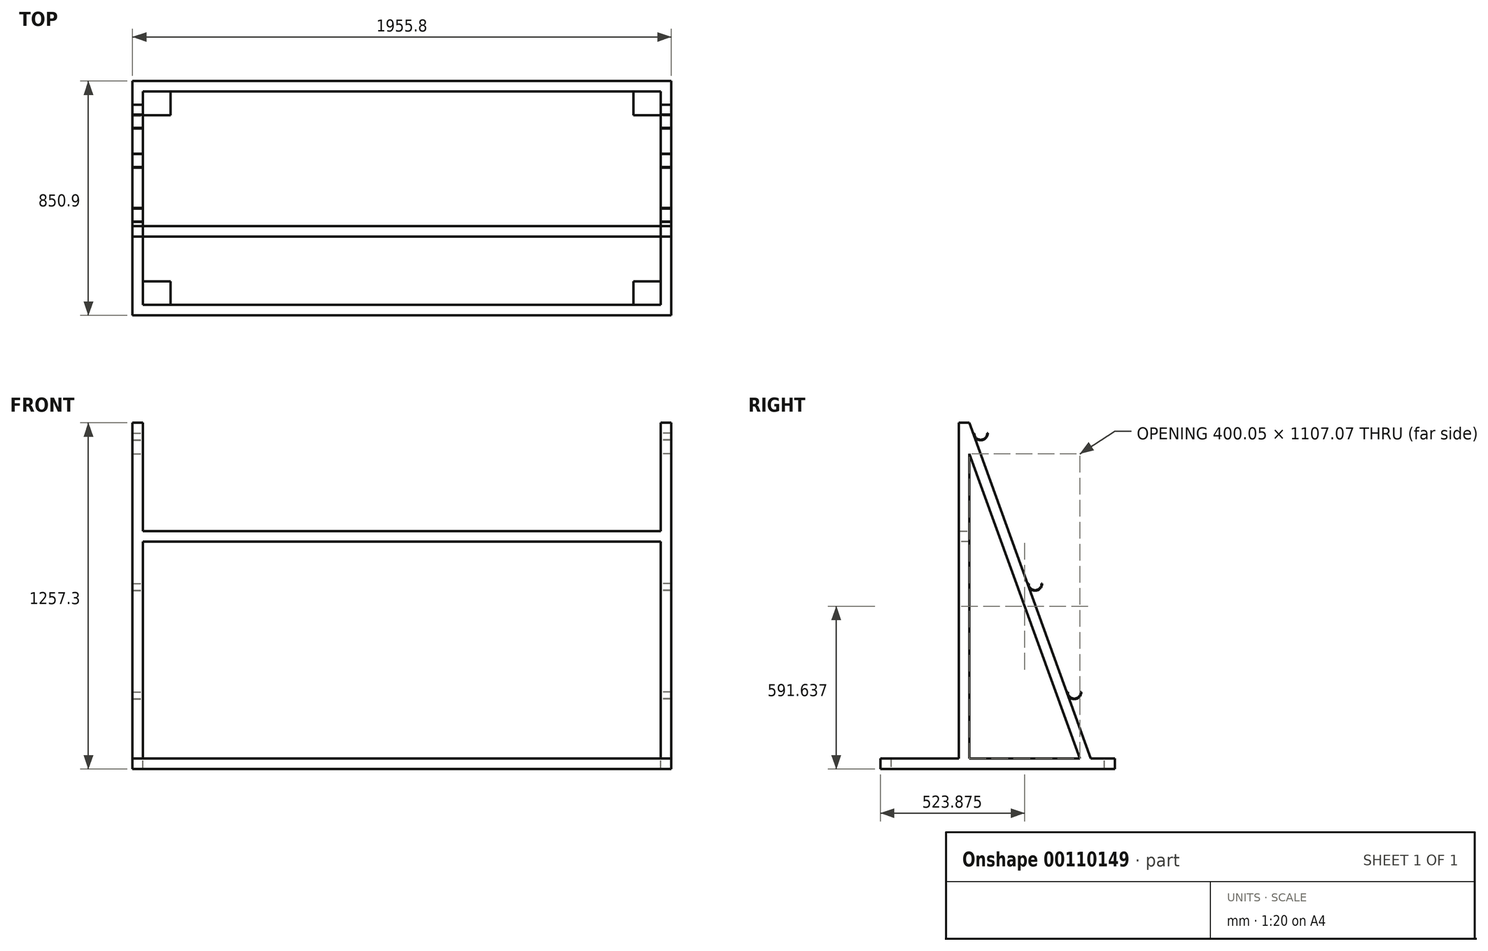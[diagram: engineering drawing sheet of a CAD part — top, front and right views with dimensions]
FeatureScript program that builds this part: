
annotation { "Feature Type Name" : "Feature", "Feature Type Description" : "" }
export const myFeature = defineFeature(function(context is Context, id is Id, definition is map)
    precondition{}
    {
        {
            var Q0;
            Q0=qCreatedBy(makeId("Right.planeOp"),FACE);
            var sketch = newSketch(context, id + "F0", { "sketchPlane" : qUnion([Q0])});
            skLineSegment(sketch, "E0", {"start": v(0, 38.1) * mm, "end": v(0, 1145.17) * mm});
            skCircle(sketch, "E1", {"center": v(40.77, 1219.2) * mm, "radius": 228.6 * mm, "construction": true});
            skLineSegment(sketch, "E2", {"start": v(-323.85, 0) * mm, "end": v(527.05, 0) * mm});
            skCircle(sketch, "E3", {"center": v(238.1, 673.1) * mm, "radius": 168.28 * mm, "construction": true});
            skCircle(sketch, "E4", {"center": v(380.37, 279.4) * mm, "radius": 168.28 * mm, "construction": true});
            skLineSegment(sketch, "E5.0", {"start": v(-38.1, 38.1) * mm, "end": v(-38.1, 1257.3) * mm});
            skLineSegment(sketch, "E6.0", {"start": v(-323.85, 38.1) * mm, "end": v(-38.1, 38.1) * mm});
            skPoint(sketch, "E7.orphan", {"position": v(0, 0) * mm});
            skLineSegment(sketch, "E8.0", {"start": v(527.05, 38.1) * mm, "end": v(527.05, 0) * mm});
            skLineSegment(sketch, "E9", {"start": v(-323.85, 38.1) * mm, "end": v(-323.85, 0) * mm});
            skLineSegment(sketch, "E10.trimOffspring", {"start": v(0, 38.1) * mm, "end": v(400.05, 38.1) * mm});
            skLineSegment(sketch, "E11.trimOffspring", {"start": v(440.56, 38.1) * mm, "end": v(527.05, 38.1) * mm});
            skLineSegment(sketch, "E12.0", {"start": v(-38.1, 1257.3) * mm, "end": v(0, 1257.3) * mm});
            skLineSegment(sketch, "E13", {"start": v(0, 1257.3) * mm, "end": v(440.56, 38.1) * mm});
            skLineSegment(sketch, "E14.0", {"start": v(0, 1145.17) * mm, "end": v(400.05, 38.1) * mm});
            skLineSegment(sketch, "E15.0", {"start": v(23.88, 1265.93) * mm, "end": v(464.45, 46.73) * mm, "construction": true});
            skLineSegment(sketch, "E16", {"start": v(40.77, 1219.2) * mm, "end": v(40.77, 1219.2) * mm});
            skLineSegment(sketch, "E17", {"start": v(238.1, 673.1) * mm, "end": v(238.1, 673.1) * mm});
            skLineSegment(sketch, "E18", {"start": v(380.37, 279.4) * mm, "end": v(380.37, 279.4) * mm});
            skSolve(sketch);
        }
        {
            var Q0;
            Q0 = qSketchRegion(id + "F0", true);
            extrude(context, id + "F1", {"entities" : qUnion([Q0]), "depth" : 38.1 * mm});
        }
        {
            var Q0;
            Q0=qCreatedBy(makeId("Right.planeOp"),FACE);
            cPlane(context, id + "F2", {"entities" : qUnion([Q0]), "cplaneType" : CPlaneType.OFFSET, "offset" : 939.8 * mm, "oppositeDirection" : true, "width" : 152.4 * mm, "height" : 152.4 * mm});
        }
        {
            var Q0;
            Q0=makeQuery(id+"F1.opExtrude","SWEPT_BODY",BODY,{"disambiguationData":[OSD([sQuery(id+"F0.wireOp",EDGE,"E0"),sQuery(id+"F0.wireOp",EDGE,"E2"),sQuery(id+"F0.wireOp",EDGE,"E5.0"),sQuery(id+"F0.wireOp",EDGE,"E6.0"),sQuery(id+"F0.wireOp",EDGE,"f51a7655-22c9-473e-9285-b1b97efc2238.0"),sQuery(id+"F0.wireOp",EDGE,"ead02582-4cc7-4f6f-915c-1df2db1e80be.0"),sQuery(id+"F0.wireOp",EDGE,"3IrbcwRK-jniz-JPX0-W7fm-mpI4lOduA6qP"),sQuery(id+"F0.wireOp",EDGE,"E8.0"),sQuery(id+"F0.wireOp",EDGE,"E9"),sQuery(id+"F0.wireOp",EDGE,"E10.trimOffspring"),sQuery(id+"F0.wireOp",EDGE,"E11.trimOffspring")])]});
            var Q1;
            Q1=qCreatedBy(id+"F2.planeOp",FACE);
            mirror(context, id + "F3", {"entities" : qUnion([Q0]), "mirrorPlane" : qUnion([Q1])});
        }
        {
            var Q0;
            Q0=qCreatedBy(makeId("Right.planeOp"),FACE);
            var sketch = newSketch(context, id + "F4", { "sketchPlane" : qUnion([Q0])});
            skLineSegment(sketch, "E19.0", {"start": v(-323.85, 38.1) * mm, "end": v(-323.85, 0) * mm});
            skLineSegment(sketch, "E20", {"start": v(-323.85, 38.1) * mm, "end": v(-285.75, 38.1) * mm});
            skLineSegment(sketch, "E21", {"start": v(-285.75, 38.1) * mm, "end": v(-285.75, 0) * mm});
            skLineSegment(sketch, "E22", {"start": v(-285.75, 0) * mm, "end": v(-323.85, 0) * mm});
            skLineSegment(sketch, "E23", {"start": v(527.05, 0) * mm, "end": v(488.95, 0) * mm});
            skLineSegment(sketch, "E24", {"start": v(488.95, 0) * mm, "end": v(488.95, 38.1) * mm});
            skLineSegment(sketch, "E25", {"start": v(488.95, 38.1) * mm, "end": v(527.05, 38.1) * mm});
            skLineSegment(sketch, "E26", {"start": v(527.05, 38.1) * mm, "end": v(527.05, 0) * mm});
            skSolve(sketch);
        }
        {
            var Q0;
            Q0 = qSketchRegion(id + "F4", true);
            var Q1;
            Q1=makeQuery(id+"F3.opPattern","COPY",FACE,{"derivedFrom":makeQuery(id+"F1.opExtrude","CAP_FACE",FACE,{"disambiguationData":[OSD([sQuery(id+"F0.wireOp",EDGE,"E0"),sQuery(id+"F0.wireOp",EDGE,"E2"),sQuery(id+"F0.wireOp",EDGE,"E5.0"),sQuery(id+"F0.wireOp",EDGE,"E6.0"),sQuery(id+"F0.wireOp",EDGE,"f51a7655-22c9-473e-9285-b1b97efc2238.0"),sQuery(id+"F0.wireOp",EDGE,"ead02582-4cc7-4f6f-915c-1df2db1e80be.0"),sQuery(id+"F0.wireOp",EDGE,"3IrbcwRK-jniz-JPX0-W7fm-mpI4lOduA6qP"),sQuery(id+"F0.wireOp",EDGE,"E8.0"),sQuery(id+"F0.wireOp",EDGE,"E9"),sQuery(id+"F0.wireOp",EDGE,"E10.trimOffspring"),sQuery(id+"F0.wireOp",EDGE,"E11.trimOffspring")])],"isStart":true}),"instanceName":"1"});
            extrude(context, id + "F5", {"entities" : qUnion([Q0]), "operationType" : NewBodyOperationType.ADD, "endBound" : BoundingType.UP_TO_SURFACE, "oppositeDirection" : true, "endBoundEntityFace" : qUnion([Q1]), "depth" : 25.4 * mm});
        }
        {
            var Q0;
            Q0=qCreatedBy(makeId("Right.planeOp"),FACE);
            var sketch = newSketch(context, id + "F6", { "sketchPlane" : qUnion([Q0])});
            skLineSegment(sketch, "E27", {"start": v(-38.1, 863.6) * mm, "end": v(0, 863.6) * mm});
            skLineSegment(sketch, "E28", {"start": v(0, 863.6) * mm, "end": v(0, 825.5) * mm});
            skLineSegment(sketch, "E29", {"start": v(0, 825.5) * mm, "end": v(-38.1, 825.5) * mm});
            skLineSegment(sketch, "E30", {"start": v(-38.1, 825.5) * mm, "end": v(-38.1, 863.6) * mm});
            skSolve(sketch);
        }
        {
            var Q0;
            Q0 = qSketchRegion(id + "F6", true);
            var Q1;
            Q1=makeQuery(id+"F3.opPattern","COPY",FACE,{"derivedFrom":makeQuery(id+"F1.opExtrude","CAP_FACE",FACE,{"disambiguationData":[OSD([sQuery(id+"F0.wireOp",EDGE,"E0"),sQuery(id+"F0.wireOp",EDGE,"E2"),sQuery(id+"F0.wireOp",EDGE,"E5.0"),sQuery(id+"F0.wireOp",EDGE,"E6.0"),sQuery(id+"F0.wireOp",EDGE,"f51a7655-22c9-473e-9285-b1b97efc2238.0"),sQuery(id+"F0.wireOp",EDGE,"ead02582-4cc7-4f6f-915c-1df2db1e80be.0"),sQuery(id+"F0.wireOp",EDGE,"3IrbcwRK-jniz-JPX0-W7fm-mpI4lOduA6qP"),sQuery(id+"F0.wireOp",EDGE,"E8.0"),sQuery(id+"F0.wireOp",EDGE,"E9"),sQuery(id+"F0.wireOp",EDGE,"E10.trimOffspring"),sQuery(id+"F0.wireOp",EDGE,"E11.trimOffspring")])],"isStart":true}),"instanceName":"1"});
            extrude(context, id + "F7", {"entities" : qUnion([Q0]), "operationType" : NewBodyOperationType.ADD, "endBound" : BoundingType.UP_TO_SURFACE, "oppositeDirection" : true, "endBoundEntityFace" : qUnion([Q1]), "depth" : 25.4 * mm});
        }
        {
            var Q0;
            Q0=qCreatedBy(makeId("Right.planeOp"),FACE);
            var sketch = newSketch(context, id + "F8", { "sketchPlane" : qUnion([Q0])});
            skLineSegment(sketch, "E31", {"start": v(66.17, 1219.2) * mm, "end": v(64.14, 1219.2) * mm});
            skLineSegment(sketch, "E32", {"start": v(263.5, 673.1) * mm, "end": v(261.47, 673.1) * mm});
            skLineSegment(sketch, "E33.trimOffspring", {"start": v(214.74, 673.1) * mm, "end": v(212.7, 673.1) * mm});
            skLineSegment(sketch, "E34", {"start": v(405.77, 279.4) * mm, "end": v(403.74, 279.4) * mm});
            skLineSegment(sketch, "E35.0", {"start": v(0, 1257.3) * mm, "end": v(440.56, 38.1) * mm, "construction": true});
            skArc(sketch, "E36", {"start": v(15.37, 1219.2) * mm, "mid": v(40.77, 1193.8) * mm, "end": v(66.17, 1219.2) * mm});
            skArc(sketch, "E37", {"start": v(212.7, 673.1) * mm, "mid": v(238.1, 647.7) * mm, "end": v(263.5, 673.1) * mm});
            skArc(sketch, "E38", {"start": v(354.97, 279.4) * mm, "mid": v(380.37, 254) * mm, "end": v(405.77, 279.4) * mm});
            skArc(sketch, "E39.0", {"start": v(17.4, 1219.2) * mm, "mid": v(40.77, 1195.83) * mm, "end": v(64.14, 1219.2) * mm});
            skLineSegment(sketch, "E40.trimOffspring", {"start": v(17.4, 1219.2) * mm, "end": v(15.37, 1219.2) * mm});
            skArc(sketch, "E41.0", {"start": v(214.74, 673.1) * mm, "mid": v(238.1, 649.73) * mm, "end": v(261.47, 673.1) * mm});
            skArc(sketch, "E42.0", {"start": v(357, 279.4) * mm, "mid": v(380.37, 256.03) * mm, "end": v(403.74, 279.4) * mm});
            skLineSegment(sketch, "E43.trimOffspring", {"start": v(357, 279.4) * mm, "end": v(354.97, 279.4) * mm});
            skSolve(sketch);
        }
        {
            var Q0;
            Q0 = qSketchRegion(id + "F8", true);
            var Q1;
            Q1 = qConstructionFilter(qBodyType(qCreatedBy(id + "F8" ,EDGE), BodyType.WIRE), ConstructionObject.NO);
            extrude(context, id + "F9", {"entities" : qUnion([Q0]), "surfaceEntities" : qUnion([Q1]), "depth" : 38.1 * mm});
        }
        {
            var Q0;
            Q0=makeQuery(id+"F9.opExtrude","SWEPT_BODY",BODY,{"disambiguationData":[OSD([sQuery(id+"F8.wireOp",EDGE,"E31"),sQuery(id+"F8.wireOp",EDGE,"ZDofccNw-4ZfO-dmuV-pbSw-bAVB7Yaiu9Kf"),sQuery(id+"F8.wireOp",EDGE,"22919390-11eb-487e-ae2f-7cb52f59a446.0"),sQuery(id+"F8.wireOp",EDGE,"0579ebcf-43b3-493b-bf73-17914a9bea4c.trimOffspring")])]});
            var Q1;
            Q1=makeQuery(id+"F9.opExtrude","SWEPT_BODY",BODY,{"disambiguationData":[OSD([sQuery(id+"F8.wireOp",EDGE,"E32"),sQuery(id+"F8.wireOp",EDGE,"87b6ec65-543f-47e7-8c87-a628fdf2dd66"),sQuery(id+"F8.wireOp",EDGE,"cc4df37b-d0ea-4d3f-8693-fb8e5ee9ca57.0"),sQuery(id+"F8.wireOp",EDGE,"E33.trimOffspring")])]});
            var Q2;
            Q2=makeQuery(id+"F9.opExtrude","SWEPT_BODY",BODY,{"disambiguationData":[OSD([sQuery(id+"F8.wireOp",EDGE,"E34"),sQuery(id+"F8.wireOp",EDGE,"1dd57ee8-0f94-4f5c-8b39-921348b20543"),sQuery(id+"F8.wireOp",EDGE,"702db500-f6c8-4907-98ad-1839e4f6e47e.0"),sQuery(id+"F8.wireOp",EDGE,"9adcec75-3f2d-4527-a6dc-758a4bda7f76.trimOffspring")])]});
            var Q3;
            Q3=qCreatedBy(id+"F2.planeOp",FACE);
            mirror(context, id + "F10", {"operationType" : NewBodyOperationType.ADD, "entities" : qUnion([Q0, Q1, Q2]), "mirrorPlane" : qUnion([Q3])});
        }
        {
            var Q0;
            {var subQ0=makeQuery(id+"F1.opExtrude","SWEPT_FACE",FACE,{"disambiguationData":[OSD([sQuery(id+"F0.wireOp",EDGE,"E2")])]});Q0=makeQuery(id+"F5.boolean.opBoolean","MERGE",FACE,{"derivedFrom":[subQ0,makeQuery(id+"F3.opPattern","COPY",FACE,{"derivedFrom":subQ0,"instanceName":"1"}),makeQuery(id+"F5.opExtrude","SWEPT_FACE",FACE,{"disambiguationData":[OSD([sQuery(id+"F4.wireOp",EDGE,"E22")])]}),makeQuery(id+"F5.opExtrude","SWEPT_FACE",FACE,{"disambiguationData":[OSD([sQuery(id+"F4.wireOp",EDGE,"E23")])]})]});}
            var sketch = newSketch(context, id + "F11", { "sketchPlane" : qUnion([Q0])});
            skLineSegment(sketch, "E44.0", {"start": v(-100.01, 285.75) * mm, "end": v(0, 285.75) * mm});
            skLineSegment(sketch, "E45", {"start": v(0, 285.75) * mm, "end": v(0, 200.03) * mm});
            skLineSegment(sketch, "E46", {"start": v(0, 200.03) * mm, "end": v(-100.01, 200.03) * mm});
            skLineSegment(sketch, "E47", {"start": v(-100.01, 200.03) * mm, "end": v(-100.01, 285.75) * mm});
            skPoint(sketch, "E48.visualSharp", {"position": v(-100.01, 200.03) * mm});
            skLineSegment(sketch, "E49", {"start": v(0, -488.95) * mm, "end": v(-100.01, -488.95) * mm});
            skLineSegment(sketch, "E50", {"start": v(-100.01, -488.95) * mm, "end": v(-100.01, -403.23) * mm});
            skLineSegment(sketch, "E51", {"start": v(-100.01, -403.23) * mm, "end": v(0, -403.23) * mm});
            skLineSegment(sketch, "E52", {"start": v(0, -403.23) * mm, "end": v(0, -488.95) * mm});
            skSolve(sketch);
        }
        {
            var Q0;
            Q0 = qSketchRegion(id + "F11", true);
            extrude(context, id + "F12", {"entities" : qUnion([Q0]), "oppositeDirection" : true, "depth" : 1.52 * mm});
        }
        {
            var Q0;
            Q0=makeQuery(id+"F12.opExtrude","SWEPT_BODY",BODY,{"disambiguationData":[OSD([sQuery(id+"F11.wireOp",EDGE,"E49"),sQuery(id+"F11.wireOp",EDGE,"E50"),sQuery(id+"F11.wireOp",EDGE,"E51"),sQuery(id+"F11.wireOp",EDGE,"E52")])]});
            var Q1;
            Q1=makeQuery(id+"F12.opExtrude","SWEPT_BODY",BODY,{"disambiguationData":[OSD([sQuery(id+"F11.wireOp",EDGE,"E45"),sQuery(id+"F11.wireOp",EDGE,"E46"),sQuery(id+"F11.wireOp",EDGE,"E47"),sQuery(id+"F11.wireOp",EDGE,"E44.0")])]});
            var Q2;
            Q2=qCreatedBy(id+"F2.planeOp",FACE);
            mirror(context, id + "F13", {"operationType" : NewBodyOperationType.ADD, "entities" : qUnion([Q0, Q1]), "mirrorPlane" : qUnion([Q2])});
        }
    });
